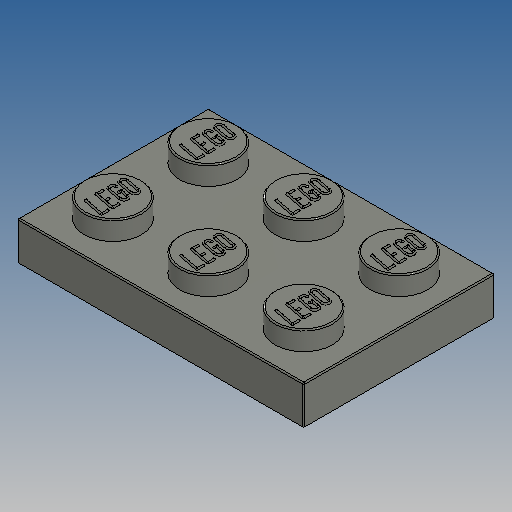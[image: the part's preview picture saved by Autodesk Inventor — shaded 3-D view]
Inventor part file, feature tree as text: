
AUTODESK INVENTOR PART (.ipt)
format: ipt  version: 2025 (Build 290162010, 162A)  size: 1,655,296 bytes
history: native  units: in
note: dims shown in document units (in); Inventor stores cm internally (conversion verified against a paired STEP export)
features: extrude x4, sketch x4, fillet x2, pattern_linear x2, other x1
ambient origin geometry x8: Origin, YZ Plane, XZ Plane, XY Plane, X Axis, Y Axis, Z Axis, Center Point
bodies: Solid1 (feature_tree)
feature tree (13):
  extrude  "Extrusion1"  Depth=0.6299in
  extrude  "Extrusion4"  Depth=0.063in
  other  "LEGO:1"
  fillet  "Fillet2"  Radius=0.063in
  pattern_linear  "Rectangular Pattern1"  Spacing1=0.189in  [1 undecoded]
  sketch  "Sketch3"  dims[d4=0.126in d5=0.0in d7=0.0591in d8=0.063in d11=0.063in d12=0.0in]
  extrude  "Extrusion2"  Depth=0.063in
  extrude  "Extrusion5"  Depth=0.189in
  pattern_linear  "Rectangular Pattern2"  Spacing1=0.1575in  [1 undecoded]
  fillet  "Fillet1"  Radius=0.1575in
  sketch  "Sketch2"  dims[d0=0.9449in d1=0.6299in]
  sketch  "Sketch9"  dims[d22=0.0039in]
  sketch  "Sketch10"  dims[d60=0.2564in d61=0.189in d62=0.063in d63=0.189in d64=0.1575in d65=0.1575in d66=0.063in d67=0.0in d68=0.0039in d69=1.1811in d71=0.315in d72=0.7874in d74=0.315in d75=0.315in d76=0.315in d77=0.0709in d78=0.0in d79=0.7874in d81=0.315in d82=0.3937in d84=0.315in d85=0.0in d86=0.0in d87=0.0in d88=0.0in d89=0.0in d90=0.0in d91=0.0in d92=0.0079in d93=0.0732in d94=0.0281in d95=0.035in d96=0.0079in d97=0.0139in d98=0.0281in d99=0.035in d100=0.0281in d101=0.0159in d102=0.0177in d103=0.035in d104=0.5428in]
note: 2 required parameter values undecoded (feature->parameter linkage not recoverable at this tier; creation-order binding heuristic only, values carry confidence <= 0.55)
